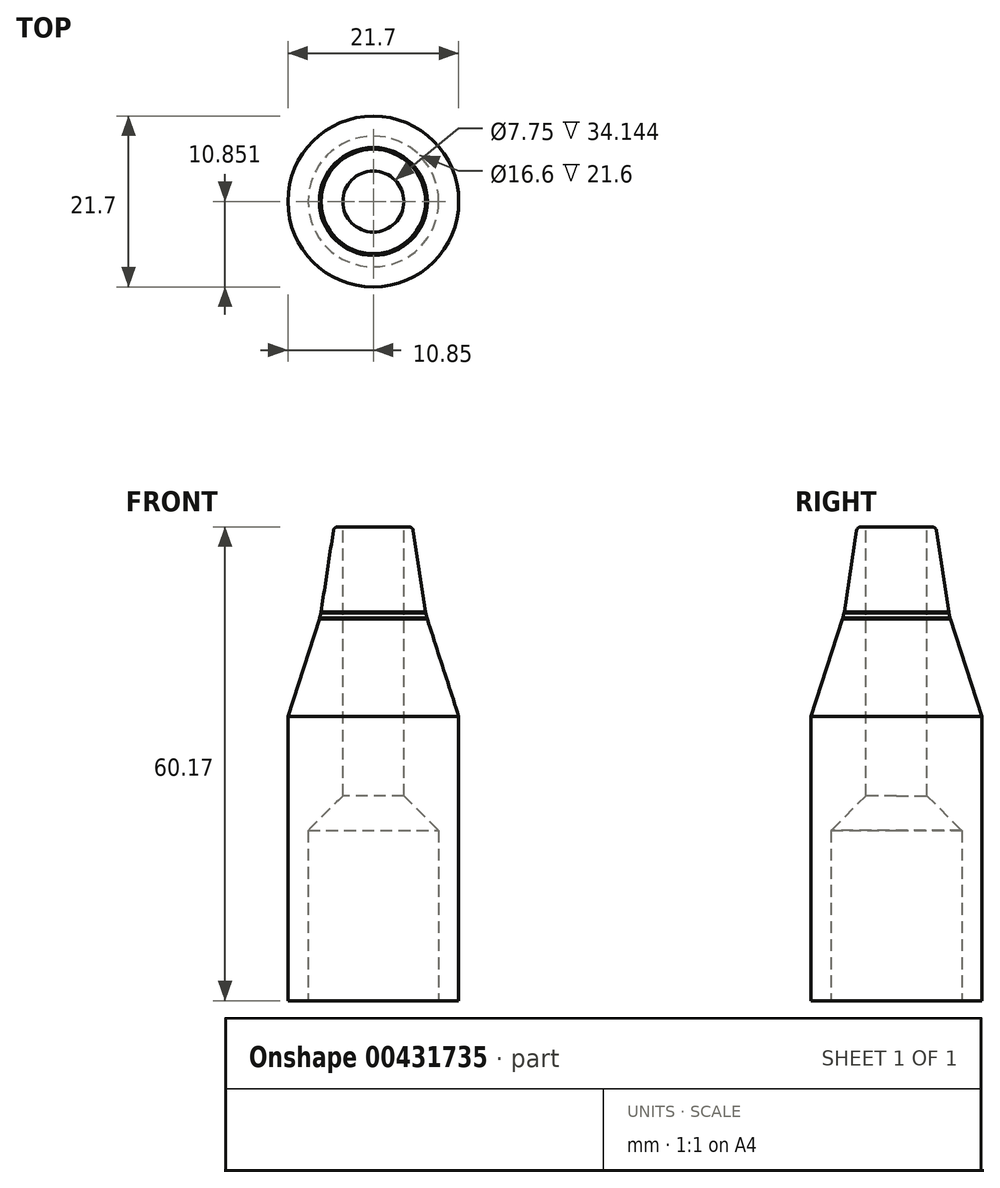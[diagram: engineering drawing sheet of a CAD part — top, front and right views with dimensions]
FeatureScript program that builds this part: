
annotation { "Feature Type Name" : "Feature", "Feature Type Description" : "" }
export const myFeature = defineFeature(function(context is Context, id is Id, definition is map)
    precondition{}
    {
        {
            var Q0;
            Q0=qCreatedBy(makeId("Right.planeOp"),FACE);
            var sketch = newSketch(context, id + "F0", { "sketchPlane" : qUnion([Q0])});
            skLineSegment(sketch, "E0", {"start": v(-22.03, 52.29) * mm, "end": v(-23.74, 41.04) * mm});
            skLineSegment(sketch, "E1", {"start": v(-23.74, 41.04) * mm, "end": v(-27.88, 28.22) * mm});
            skLineSegment(sketch, "E2", {"start": v(-27.88, 28.22) * mm, "end": v(-27.88, -7.88) * mm});
            skLineSegment(sketch, "E3", {"start": v(-22.03, 52.29) * mm, "end": v(-17.03, 52.29) * mm});
            skLineSegment(sketch, "E4", {"start": v(-17.03, 52.29) * mm, "end": v(-17.03, -7.88) * mm});
            skLineSegment(sketch, "E5", {"start": v(-17.03, -7.88) * mm, "end": v(-27.88, -7.88) * mm});
            skSolve(sketch);
        }
        {
            var Q0;
            Q0=makeQuery(id+"F0.imprint","IMPRINT",FACE,{"disambiguationData":[TD([[makeQuery(id+"F0.imprint","IMPRINT",EDGE,{"derivedFrom":sQuery(id+"F0.wireOp",EDGE,"E0")}),1.0]])]});
            var Q1;
            Q1=sQuery(id+"F0.wireOp",EDGE,"E4");
            revolve(context, id + "F1", {"entities" : qUnion([Q0]), "axis" : qUnion([Q1]), "revolveType" : RevolveType.FULL});
        }
        {
            var Q0;
            Q0=makeQuery(id+"F1.opRevolve","SWEPT_FACE",FACE,{"disambiguationData":[OSD([sQuery(id+"F0.wireOp",EDGE,"E3")])]});
            var sketch = newSketch(context, id + "F2", { "sketchPlane" : qUnion([Q0])});
            skCircle(sketch, "E6", {"center": v(0, -17.03) * mm, "radius": 3.87 * mm});
            skSolve(sketch);
        }
        {
            var Q0;
            Q0 = qSketchRegion(id + "F2", true);
            extrude(context, id + "F3", {"entities" : qUnion([Q0]), "operationType" : NewBodyOperationType.REMOVE, "oppositeDirection" : true, "depth" : 90.7 * mm});
        }
        {
            var Q0;
            Q0=makeQuery(id+"F1.opRevolve","SWEPT_FACE",FACE,{"disambiguationData":[OSD([sQuery(id+"F0.wireOp",EDGE,"E5")])]});
            var sketch = newSketch(context, id + "F4", { "sketchPlane" : qUnion([Q0])});
            skCircle(sketch, "E7", {"center": v(0, 17.03) * mm, "radius": 8.3 * mm});
            skSolve(sketch);
        }
        {
            var Q0;
            Q0 = qSketchRegion(id + "F4", true);
            extrude(context, id + "F5", {"entities" : qUnion([Q0]), "operationType" : NewBodyOperationType.REMOVE, "oppositeDirection" : true, "depth" : 26.6 * mm});
        }
        {
            var Q0;
            Q0=makeQuery(id+"F5.boolean.opBoolean","COPY",EDGE,{"derivedFrom":makeQuery(id+"F5.opExtrude","CAP_EDGE",EDGE,{"disambiguationData":[OSD([sQuery(id+"F4.wireOp",EDGE,"E7")])],"isStart":false})});
            chamfer(context, id + "F6", {"entities" : qUnion([Q0]), "width" : 5 * mm, "tangentPropagation" : true});
        }
        {
            var Q0;
            Q0=makeQuery(id+"F1.opRevolve","SWEPT_EDGE",EDGE,{"disambiguationData":[OSD([sQuery(id+"F0.wireOp",EDGE,"E0"),sQuery(id+"F0.wireOp",EDGE,"E3")])]});
            var Q1;
            Q1=makeQuery(id+"F3.boolean.opBoolean","COPY",EDGE,{"derivedFrom":makeQuery(id+"F3.opExtrude","CAP_EDGE",EDGE,{"disambiguationData":[OSD([sQuery(id+"F2.wireOp",EDGE,"E6")])],"isStart":true})});
            fillet(context, id + "F7", {"entities" : qUnion([Q0, Q1]), "radius" : 0.5 * mm, "tangentPropagation" : true, "allowEdgeOverflow" : false});
        }
        {
            var Q0;
            Q0=makeQuery(id+"F1.opRevolve","SWEPT_EDGE",EDGE,{"disambiguationData":[OSD([sQuery(id+"F0.wireOp",EDGE,"E0"),sQuery(id+"F0.wireOp",EDGE,"E1")])]});
            chamfer(context, id + "F8", {"entities" : qUnion([Q0]), "width" : 5 * mm, "tangentPropagation" : true});
        }
        {
            var Q0;
            {var subQ0=sQuery(id+"F0.wireOp",EDGE,"E1");Q0=makeQuery(id+"F8.opChamfer","BLEND_EDGE",EDGE,{"blendedFrom":[makeQuery(id+"F1.opRevolve","SWEPT_EDGE",EDGE,{"disambiguationData":[OSD([sQuery(id+"F0.wireOp",EDGE,"E0"),subQ0])]}),makeQuery(id+"F1.opRevolve","SWEPT_FACE",FACE,{"disambiguationData":[OSD([subQ0])]})],"blendedInto":[makeQuery(id+"F1.opRevolve","SWEPT_FACE",FACE,{"disambiguationData":[OSD([subQ0])]})]});}
            var Q1;
            {var subQ0=sQuery(id+"F0.wireOp",EDGE,"E0");Q1=makeQuery(id+"F8.opChamfer","BLEND_EDGE",EDGE,{"blendedFrom":[makeQuery(id+"F1.opRevolve","SWEPT_EDGE",EDGE,{"disambiguationData":[OSD([subQ0,sQuery(id+"F0.wireOp",EDGE,"E1")])]}),makeQuery(id+"F1.opRevolve","SWEPT_FACE",FACE,{"disambiguationData":[OSD([subQ0])]})],"blendedInto":[makeQuery(id+"F1.opRevolve","SWEPT_FACE",FACE,{"disambiguationData":[OSD([subQ0])]})]});}
            chamfer(context, id + "F9", {"entities" : qUnion([Q0, Q1]), "width" : 2 * mm, "tangentPropagation" : true});
        }
    });
